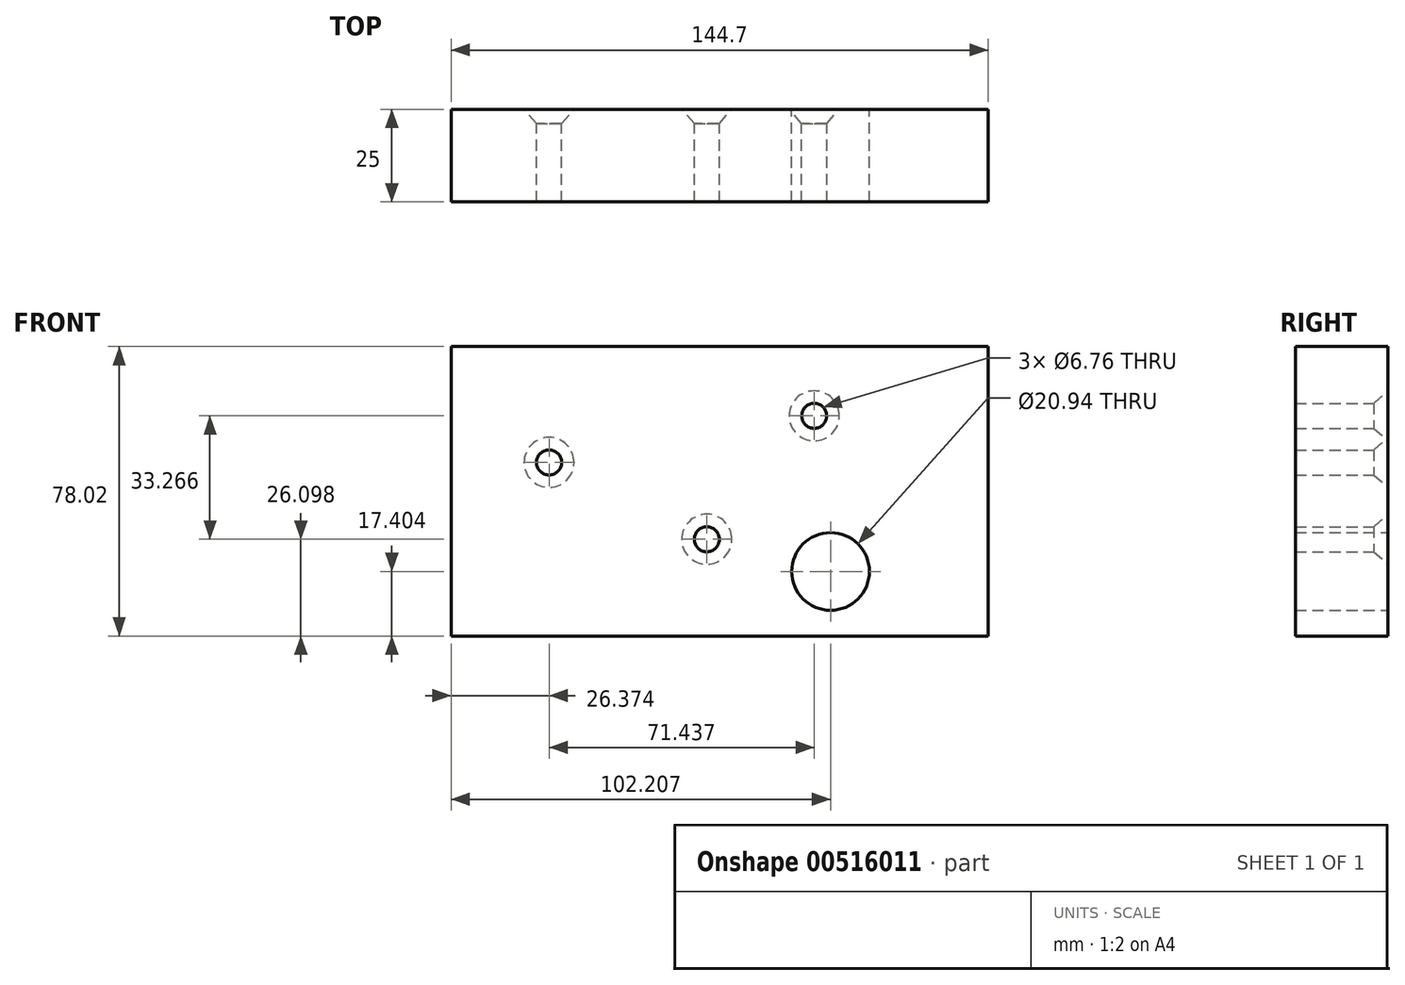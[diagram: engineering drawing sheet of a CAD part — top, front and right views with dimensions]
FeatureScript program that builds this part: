
annotation { "Feature Type Name" : "Feature", "Feature Type Description" : "" }
export const myFeature = defineFeature(function(context is Context, id is Id, definition is map)
    precondition{}
    {
        {
            var Q0;
            Q0=qCreatedBy(makeId("Front.planeOp"),FACE);
            var sketch = newSketch(context, id + "F0", { "sketchPlane" : qUnion([Q0])});
            skLineSegment(sketch, "E0.bottom", {"start": v(-124.92, 26.4) * mm, "end": v(19.78, 26.4) * mm});
            skLineSegment(sketch, "E0.top", {"start": v(-124.92, -51.62) * mm, "end": v(19.78, -51.62) * mm});
            skLineSegment(sketch, "E0.left", {"start": v(-124.92, 26.4) * mm, "end": v(-124.92, -51.62) * mm});
            skLineSegment(sketch, "E0.right", {"start": v(19.78, 26.4) * mm, "end": v(19.78, -51.62) * mm});
            skPoint(sketch, "E1", {"position": v(-98.55, -4.82) * mm});
            skPoint(sketch, "E2", {"position": v(-56.05, -25.52) * mm});
            skPoint(sketch, "E3", {"position": v(-27.1, 7.74) * mm});
            skCircle(sketch, "E4", {"center": v(-22.71, -34.22) * mm, "radius": 10.47 * mm});
            skCircle(sketch, "E5", {"center": v(-71.8, -2.96) * mm, "radius": 14.63 * mm});
            skSolve(sketch);
        }
        {
            var Q0;
            Q0 = qSketchRegion(id + "F0", true);
            extrude(context, id + "F1", {"entities" : qUnion([Q0]), "depth" : 25 * mm, "offsetDistance" : 25 * mm});
        }
        {
            var Q0;
            Q0=sQuery(id+"F0.wireOp",VERTEX,"E1");
            var Q1;
            Q1=sQuery(id+"F0.wireOp",VERTEX,"E2");
            var Q2;
            Q2=sQuery(id+"F0.wireOp",VERTEX,"E3");
            var Q3;
            Q3=makeQuery(id+"F1.opExtrude","SWEPT_BODY",BODY,{"disambiguationData":[OSD([sQuery(id+"F0.wireOp",EDGE,"E0.bottom"),sQuery(id+"F0.wireOp",EDGE,"E0.top"),sQuery(id+"F0.wireOp",EDGE,"E0.left"),sQuery(id+"F0.wireOp",EDGE,"E0.right"),sQuery(id+"F0.wireOp",EDGE,"E4"),sQuery(id+"F0.wireOp",EDGE,"E5")])]});
            hole(context, id + "F2", {"style" : HoleStyle.C_SINK, "endStyle" : HoleEndStyle.THROUGH, "oppositeDirection" : true, "standardTappedOrClearance" : lookupTablePath({ "standard" : "ANSI", "fit" : "Normal (ASME)", "size" : "1/4", "type" : "Clearance" }), "standardBlindInLast" : lookupTablePath({ "fit" : "Free", "standard" : "ANSI", "size" : "1/4", "type" : "Clearance" }), "holeDiameter" : 6.76 * mm, "cSinkDiameter" : 13.5 * mm, "cSinkAngle" : 82 * degree, "isTappedThrough" : true, "tappedDepth" : 12 * mm, "tapClearance" : 3, "locations" : qUnion([Q0, Q1, Q2]), "scope" : qUnion([Q3])});
        }
        {
            var Q0;
            Q0=makeQuery(id+"F0.imprint","IMPRINT",FACE,{"disambiguationData":[TD([[makeQuery(id+"F0.imprint","IMPRINT",EDGE,{"derivedFrom":sQuery(id+"F0.wireOp",EDGE,"E5")}),1.0]])]});
            extrude(context, id + "F3", {"entities" : qUnion([Q0]), "operationType" : NewBodyOperationType.ADD, "depth" : 25 * mm, "offsetDistance" : 25 * mm});
        }
    });
